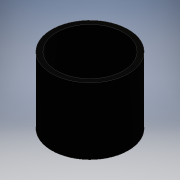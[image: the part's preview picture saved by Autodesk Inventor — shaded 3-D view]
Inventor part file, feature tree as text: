
AUTODESK INVENTOR PART (.ipt)
format: ipt  version: 2016 (Build 200138000, 138)  size: 95,232 bytes
history: native  units: mm
features: other x1, sketch x1, extrude x1
ambient origin geometry x8: Origin, YZ Plane, XZ Plane, XY Plane, X Axis, Y Axis, Z Axis, Center Point
bodies: Body1 (feature_tree)
feature tree (3):
  other  "ソリッド1"
  sketch  "スケッチ1"
  extrude  "押し出し1"  Depth=20.0mm
